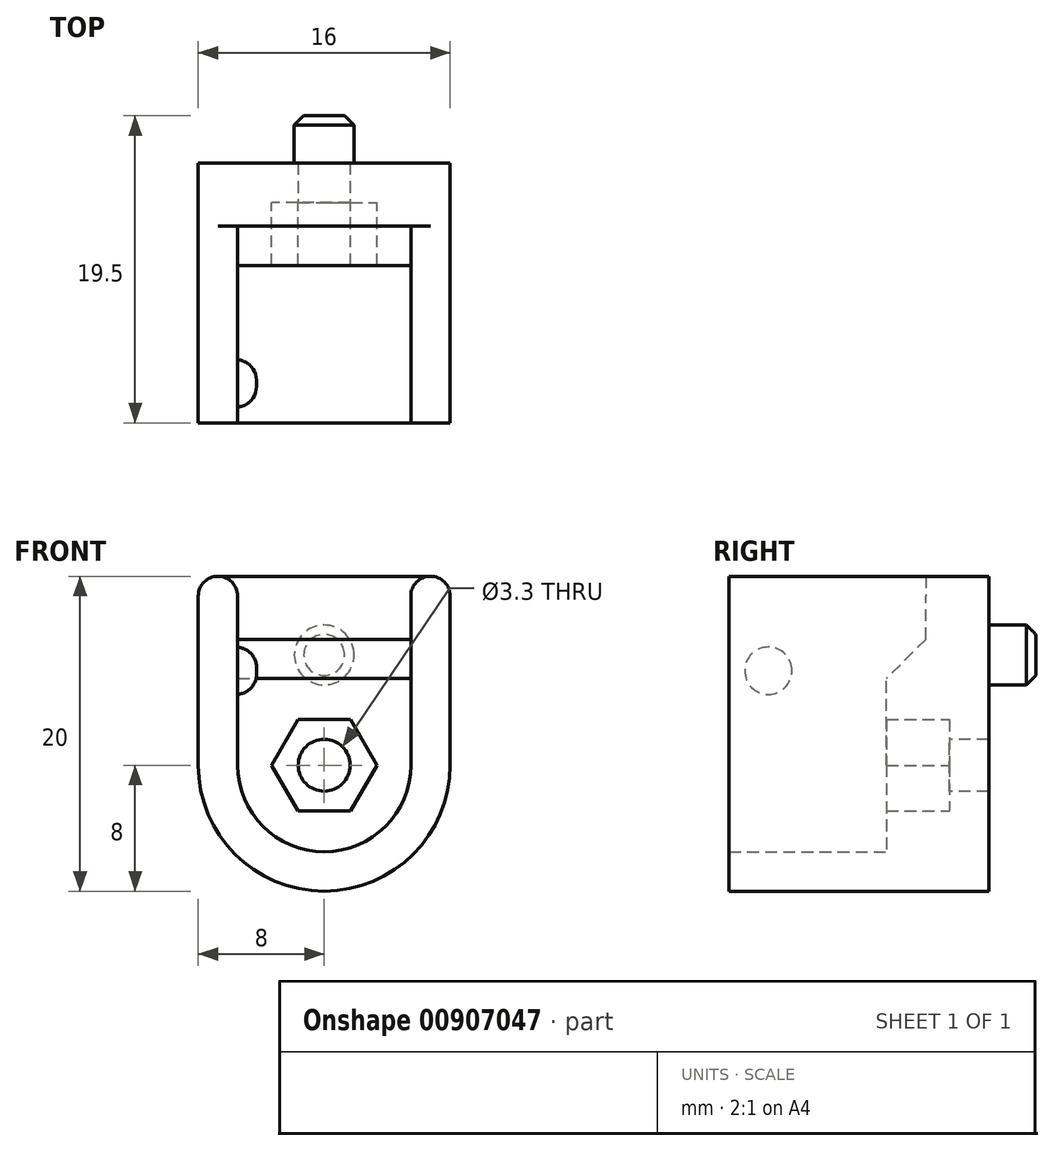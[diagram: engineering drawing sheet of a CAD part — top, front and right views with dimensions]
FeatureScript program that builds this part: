
annotation { "Feature Type Name" : "Feature", "Feature Type Description" : "" }
export const myFeature = defineFeature(function(context is Context, id is Id, definition is map)
    precondition{}
    {
        {
            var Q0;
            Q0=qCreatedBy(makeId("Front.planeOp"),FACE);
            var sketch = newSketch(context, id + "F0", { "sketchPlane" : qUnion([Q0])});
            skArc(sketch, "E0", {"start": v(8, 0) * mm, "mid": v(0, -8) * mm, "end": v(-8, 0) * mm});
            skLineSegment(sketch, "E1", {"start": v(-8, 0) * mm, "end": v(-8, 10.75) * mm});
            skArc(sketch, "E2", {"start": v(-8, 10.75) * mm, "mid": v(-7.63, 11.63) * mm, "end": v(-6.75, 12) * mm});
            skLineSegment(sketch, "E3", {"start": v(0, 0) * mm, "end": v(0, 13.45) * mm, "construction": true});
            skArc(sketch, "E4.MirrorCS", {"start": v(8, 10.75) * mm, "mid": v(7.63, 11.63) * mm, "end": v(6.75, 12) * mm});
            skLineSegment(sketch, "E5.MirrorCS", {"start": v(8, 0) * mm, "end": v(8, 10.75) * mm});
            skLineSegment(sketch, "E6", {"start": v(-6.75, 12) * mm, "end": v(6.75, 12) * mm});
            skSolve(sketch);
        }
        {
            var Q0;
            Q0 = qSketchRegion(id + "F0", true);
            extrude(context, id + "F1", {"entities" : qUnion([Q0]), "depth" : 4 * mm, "offsetDistance" : 25 * mm});
        }
        {
            var Q0;
            Q0=makeQuery(id+"F1.opExtrude","CAP_FACE",FACE,{"disambiguationData":[OSD([sQuery(id+"F0.wireOp",EDGE,"E0"),sQuery(id+"F0.wireOp",EDGE,"E1"),sQuery(id+"F0.wireOp",EDGE,"E2"),sQuery(id+"F0.wireOp",EDGE,"E4.MirrorCS"),sQuery(id+"F0.wireOp",EDGE,"E5.MirrorCS"),sQuery(id+"F0.wireOp",EDGE,"E6")])],"isStart":false});
            var sketch = newSketch(context, id + "F2", { "sketchPlane" : qUnion([Q0])});
            skArc(sketch, "E7.0", {"start": v(5.5, 0) * mm, "mid": v(0, -5.5) * mm, "end": v(-5.5, 0) * mm});
            skLineSegment(sketch, "E8", {"start": v(-5.5, 0) * mm, "end": v(-5.5, 10.75) * mm});
            skArc(sketch, "E9", {"start": v(-5.5, 10.75) * mm, "mid": v(-6.75, 12) * mm, "end": v(-8, 10.75) * mm});
            skLineSegment(sketch, "E10.0", {"start": v(-8, 0) * mm, "end": v(-8, 10.75) * mm});
            skArc(sketch, "E11.0", {"start": v(8, 0) * mm, "mid": v(0, -8) * mm, "end": v(-8, 0) * mm});
            skLineSegment(sketch, "E12", {"start": v(0, 0) * mm, "end": v(0, 17.02) * mm, "construction": true});
            skLineSegment(sketch, "E13.MirrorCS", {"start": v(5.5, 0) * mm, "end": v(5.5, 10.75) * mm});
            skArc(sketch, "E14.MirrorCS", {"start": v(5.5, 10.75) * mm, "mid": v(6.75, 12) * mm, "end": v(8, 10.75) * mm});
            skLineSegment(sketch, "E15.MirrorCS", {"start": v(8, 0) * mm, "end": v(8, 10.75) * mm});
            skSolve(sketch);
        }
        {
            var Q0;
            Q0 = qSketchRegion(id + "F2", true);
            extrude(context, id + "F3", {"entities" : qUnion([Q0]), "operationType" : NewBodyOperationType.ADD, "depth" : 12.5 * mm, "offsetDistance" : 25 * mm});
        }
        {
            var Q0;
            Q0=makeQuery(id+"F1.opExtrude","CAP_FACE",FACE,{"disambiguationData":[OSD([sQuery(id+"F0.wireOp",EDGE,"E0"),sQuery(id+"F0.wireOp",EDGE,"E1"),sQuery(id+"F0.wireOp",EDGE,"E2"),sQuery(id+"F0.wireOp",EDGE,"E4.MirrorCS"),sQuery(id+"F0.wireOp",EDGE,"E5.MirrorCS"),sQuery(id+"F0.wireOp",EDGE,"E6")])],"isStart":false});
            var sketch = newSketch(context, id + "F4", { "sketchPlane" : qUnion([Q0])});
            skLineSegment(sketch, "E16", {"start": v(-5.5, 5.5) * mm, "end": v(5.5, 5.5) * mm});
            skArc(sketch, "E17.0", {"start": v(5.5, 0) * mm, "mid": v(0, -5.5) * mm, "end": v(-5.5, 0) * mm});
            skLineSegment(sketch, "E18", {"start": v(-5.5, 0) * mm, "end": v(-5.5, 5.5) * mm});
            skLineSegment(sketch, "E19", {"start": v(5.5, 0) * mm, "end": v(5.5, 5.5) * mm});
            skCircle(sketch, "E20.cCircle", {"center": v(0, 0) * mm, "radius": 2.9 * mm, "construction": true});
            skLineSegment(sketch, "E20.0", {"start": v(1.67, 2.9) * mm, "end": v(3.35, 0) * mm});
            skLineSegment(sketch, "E20.1", {"start": v(3.35, 0) * mm, "end": v(1.67, -2.9) * mm});
            skLineSegment(sketch, "E20.2", {"start": v(1.67, -2.9) * mm, "end": v(-1.67, -2.9) * mm});
            skLineSegment(sketch, "E20.3", {"start": v(-1.67, -2.9) * mm, "end": v(-3.35, 0) * mm});
            skLineSegment(sketch, "E20.4", {"start": v(-3.35, 0) * mm, "end": v(-1.67, 2.9) * mm});
            skLineSegment(sketch, "E20.5", {"start": v(-1.67, 2.9) * mm, "end": v(1.67, 2.9) * mm});
            skPoint(sketch, "E20.0.midPoint", {"position": v(2.51, 1.45) * mm});
            skSolve(sketch);
        }
        {
            var Q0;
            Q0 = qSketchRegion(id + "F4", true);
            extrude(context, id + "F5", {"entities" : qUnion([Q0]), "operationType" : NewBodyOperationType.ADD, "depth" : 2.5 * mm, "offsetDistance" : 25 * mm});
        }
        {
            var Q0;
            Q0=makeQuery(id+"F5.boolean.opBoolean","SPLIT",FACE,{"disambiguationData":[TD([makeQuery(id+"F5.opExtrude","SWEPT_FACE",FACE,{"disambiguationData":[OSD([sQuery(id+"F4.wireOp",EDGE,"E20.0")])]})])],"derivedFrom":makeQuery(id+"F1.opExtrude","CAP_FACE",FACE,{"disambiguationData":[OSD([sQuery(id+"F0.wireOp",EDGE,"E0"),sQuery(id+"F0.wireOp",EDGE,"E1"),sQuery(id+"F0.wireOp",EDGE,"E2"),sQuery(id+"F0.wireOp",EDGE,"E4.MirrorCS"),sQuery(id+"F0.wireOp",EDGE,"E5.MirrorCS"),sQuery(id+"F0.wireOp",EDGE,"E6")])],"isStart":false})});
            var sketch = newSketch(context, id + "F6", { "sketchPlane" : qUnion([Q0])});
            skLineSegment(sketch, "E21.0", {"start": v(-1.67, -2.9) * mm, "end": v(-3.35, 0) * mm});
            skLineSegment(sketch, "E21.1", {"start": v(-3.35, 0) * mm, "end": v(-1.67, 2.9) * mm});
            skLineSegment(sketch, "E21.2", {"start": v(-1.67, 2.9) * mm, "end": v(1.67, 2.9) * mm});
            skLineSegment(sketch, "E21.3", {"start": v(1.67, 2.9) * mm, "end": v(3.35, 0) * mm});
            skLineSegment(sketch, "E21.4", {"start": v(3.35, 0) * mm, "end": v(1.67, -2.9) * mm});
            skLineSegment(sketch, "E21.5", {"start": v(1.67, -2.9) * mm, "end": v(-1.67, -2.9) * mm});
            skSolve(sketch);
        }
        {
            var Q0;
            Q0 = qSketchRegion(id + "F6", true);
            extrude(context, id + "F7", {"entities" : qUnion([Q0]), "operationType" : NewBodyOperationType.REMOVE, "oppositeDirection" : true, "depth" : 1.5 * mm, "offsetDistance" : 25 * mm});
        }
        {
            var Q0;
            Q0=makeQuery(id+"F5.opExtrude","CAP_EDGE",EDGE,{"disambiguationData":[OSD([sQuery(id+"F4.wireOp",EDGE,"E16")])],"isStart":true});
            chamfer(context, id + "F8", {"entities" : qUnion([Q0]), "width" : 2.5 * mm, "tangentPropagation" : true});
        }
        {
            var Q0;
            Q0=makeQuery(id+"F7.boolean.opBoolean","COPY",FACE,{"derivedFrom":makeQuery(id+"F7.opExtrude","CAP_FACE",FACE,{"disambiguationData":[OSD([sQuery(id+"F6.wireOp",EDGE,"E21.0"),sQuery(id+"F6.wireOp",EDGE,"E21.1"),sQuery(id+"F6.wireOp",EDGE,"E21.2"),sQuery(id+"F6.wireOp",EDGE,"E21.3"),sQuery(id+"F6.wireOp",EDGE,"E21.4"),sQuery(id+"F6.wireOp",EDGE,"E21.5")])],"isStart":false})});
            var sketch = newSketch(context, id + "F9", { "sketchPlane" : qUnion([Q0])});
            skCircle(sketch, "E22", {"center": v(0, 0) * mm, "radius": 1.65 * mm});
            skSolve(sketch);
        }
        {
            var Q0;
            Q0 = qSketchRegion(id + "F9", true);
            extrude(context, id + "F10", {"entities" : qUnion([Q0]), "operationType" : NewBodyOperationType.REMOVE, "endBound" : BoundingType.THROUGH_ALL, "oppositeDirection" : true, "depth" : 25 * mm, "offsetDistance" : 25 * mm});
        }
        {
            var Q0;
            Q0=makeQuery(id+"F1.opExtrude","CAP_FACE",FACE,{"disambiguationData":[OSD([sQuery(id+"F0.wireOp",EDGE,"E0"),sQuery(id+"F0.wireOp",EDGE,"E1"),sQuery(id+"F0.wireOp",EDGE,"E2"),sQuery(id+"F0.wireOp",EDGE,"E4.MirrorCS"),sQuery(id+"F0.wireOp",EDGE,"E5.MirrorCS"),sQuery(id+"F0.wireOp",EDGE,"E6")])],"isStart":true});
            var sketch = newSketch(context, id + "F11", { "sketchPlane" : qUnion([Q0])});
            skCircle(sketch, "E23", {"center": v(0, 7) * mm, "radius": 1.9 * mm});
            skSolve(sketch);
        }
        {
            var Q0;
            Q0 = qSketchRegion(id + "F11", true);
            extrude(context, id + "F12", {"entities" : qUnion([Q0]), "operationType" : NewBodyOperationType.ADD, "depth" : 3 * mm, "offsetDistance" : 25 * mm});
        }
        {
            var Q0;
            Q0=makeQuery(id+"F12.opExtrude","CAP_EDGE",EDGE,{"disambiguationData":[OSD([sQuery(id+"F11.wireOp",EDGE,"E23")])],"isStart":false});
            chamfer(context, id + "F13", {"entities" : qUnion([Q0]), "width" : 0.6 * mm, "tangentPropagation" : true});
        }
        {
            var Q0;
            Q0=qCreatedBy(makeId("Right.planeOp"),FACE);
            var sketch = newSketch(context, id + "F14", { "sketchPlane" : qUnion([Q0])});
            skLineSegment(sketch, "E24", {"start": v(-16.5, -5.5) * mm, "end": v(-11.2, -5.5) * mm});
            skSolve(sketch);
        }
        {
            var Q0;
            Q0=makeQuery(id+"F3.opExtrude","SWEPT_FACE",FACE,{"disambiguationData":[OSD([sQuery(id+"F2.wireOp",EDGE,"E8")])]});
            var sketch = newSketch(context, id + "F15", { "sketchPlane" : qUnion([Q0])});
            skCircle(sketch, "E25", {"center": v(-14, 6) * mm, "radius": 1.5 * mm});
            skSolve(sketch);
        }
        {
            var Q0;
            Q0 = qSketchRegion(id + "F15", true);
            extrude(context, id + "F16", {"entities" : qUnion([Q0]), "operationType" : NewBodyOperationType.ADD, "depth" : 1.2 * mm, "offsetDistance" : 25 * mm});
        }
        {
            var Q0;
            Q0=makeQuery(id+"F16.opExtrude","CAP_EDGE",EDGE,{"disambiguationData":[OSD([sQuery(id+"F15.wireOp",EDGE,"E25")])],"isStart":false});
            fillet(context, id + "F17", {"entities" : qUnion([Q0]), "radius" : 1.3 * mm, "tangentPropagation" : true, "allowEdgeOverflow" : false});
        }
    });
